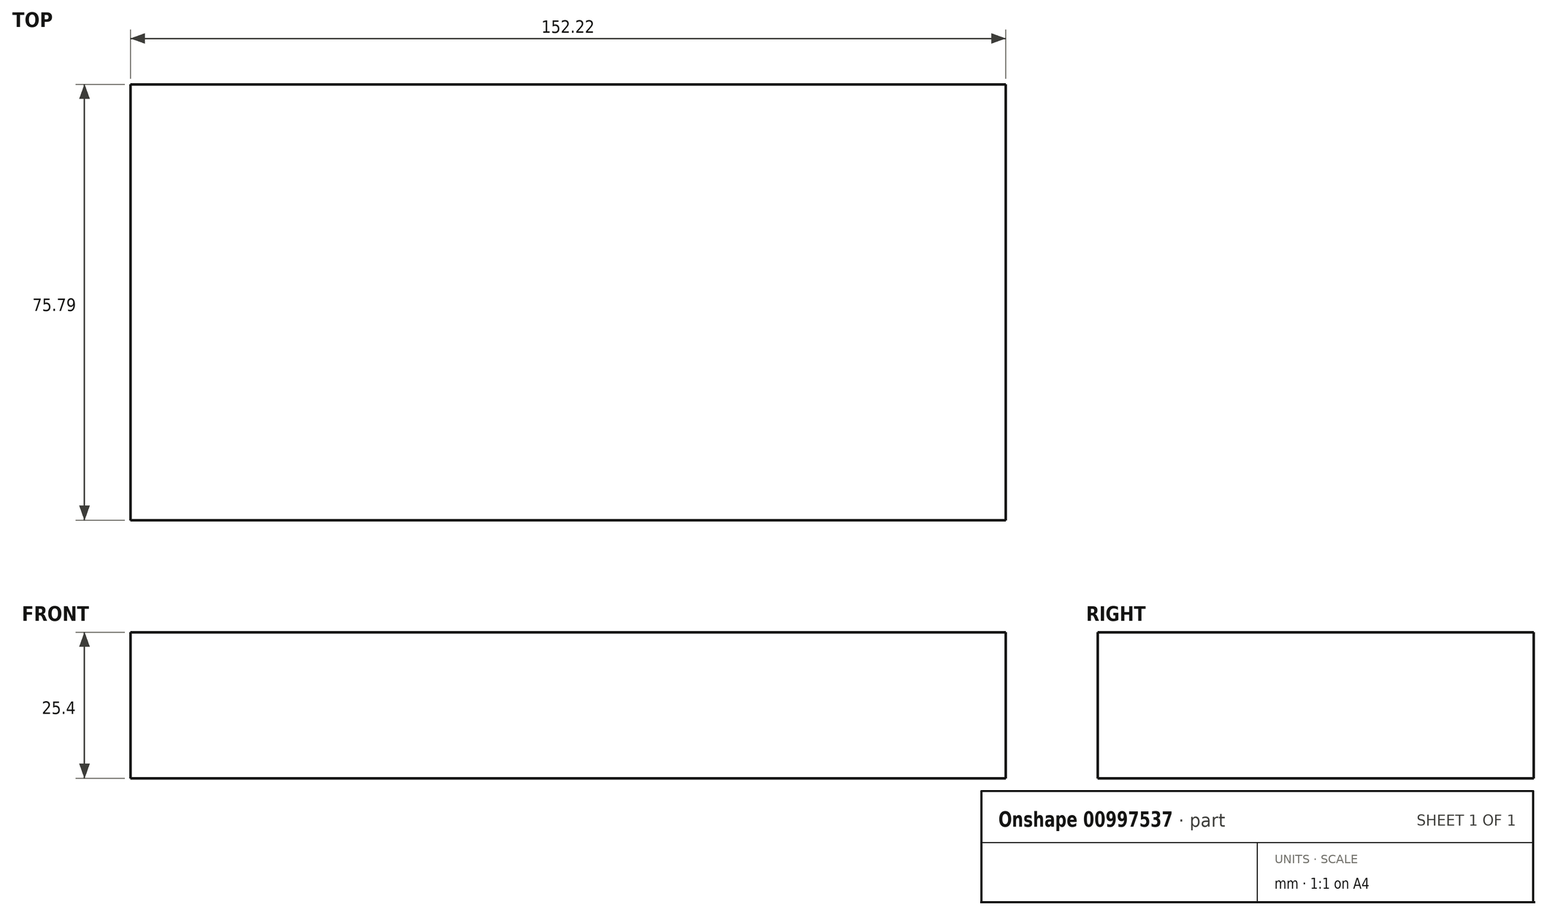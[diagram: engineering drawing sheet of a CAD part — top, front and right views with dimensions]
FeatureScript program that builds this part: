
annotation { "Feature Type Name" : "Feature", "Feature Type Description" : "" }
export const myFeature = defineFeature(function(context is Context, id is Id, definition is map)
    precondition{}
    {
        {
            var Q0;
            Q0=qCreatedBy(makeId("Top.planeOp"),FACE);
            var sketch = newSketch(context, id + "F0", { "sketchPlane" : qUnion([Q0])});
            skLineSegment(sketch, "E0.bottom", {"start": v(-75.79, 0) * mm, "end": v(76.43, 0) * mm});
            skLineSegment(sketch, "E0.top", {"start": v(-75.79, 75.79) * mm, "end": v(76.43, 75.79) * mm});
            skLineSegment(sketch, "E0.left", {"start": v(-75.79, 0) * mm, "end": v(-75.79, 75.79) * mm});
            skLineSegment(sketch, "E0.right", {"start": v(76.43, 0) * mm, "end": v(76.43, 75.79) * mm});
            skSolve(sketch);
        }
        {
            var Q0;
            Q0=makeQuery(id+"F0.imprint","IMPRINT",FACE,{"disambiguationData":[TD([[makeQuery(id+"F0.imprint","IMPRINT",EDGE,{"derivedFrom":sQuery(id+"F0.wireOp",EDGE,"E0.bottom")}),1.0]])]});
            extrude(context, id + "F1", {"entities" : qUnion([Q0]), "depth" : 25.4 * mm, "offsetDistance" : 25.4 * mm});
        }
    });
